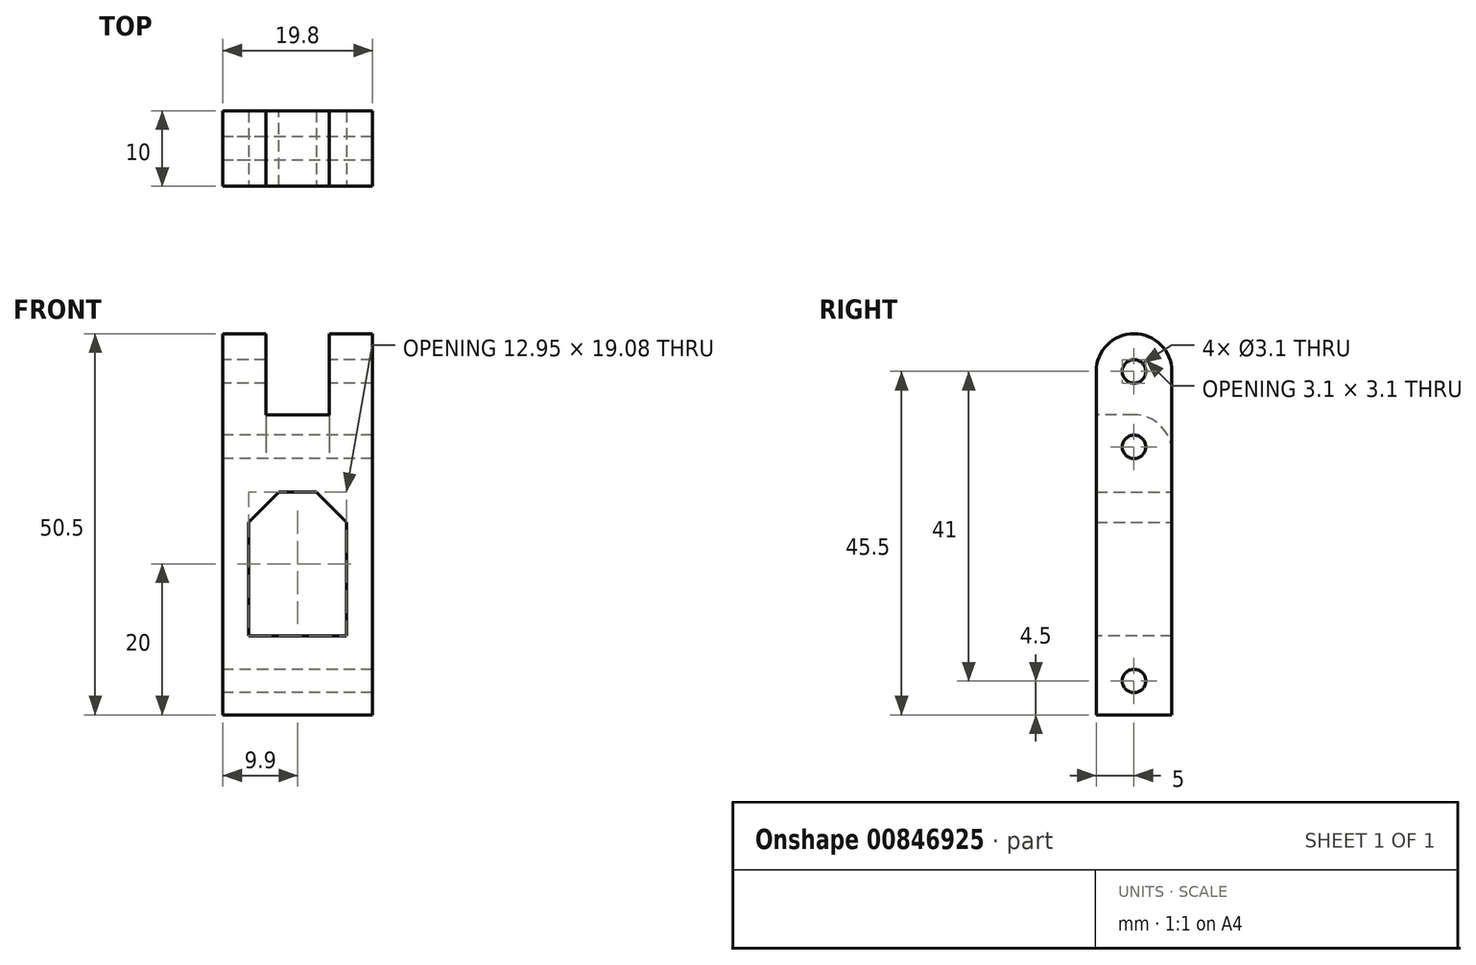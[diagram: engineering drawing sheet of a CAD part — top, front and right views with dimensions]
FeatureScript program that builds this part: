
annotation { "Feature Type Name" : "Feature", "Feature Type Description" : "" }
export const myFeature = defineFeature(function(context is Context, id is Id, definition is map)
    precondition{}
    {
        {
            var Q0;
            Q0=qCreatedBy(makeId("Right.planeOp"),FACE);
            var sketch = newSketch(context, id + "F0", { "sketchPlane" : qUnion([Q0])});
            skLineSegment(sketch, "E0.bottom", {"start": v(-5, -20) * mm, "end": v(5, -20) * mm});
            skLineSegment(sketch, "E0.top", {"start": v(-5, 25.5) * mm, "end": v(5, 25.5) * mm});
            skLineSegment(sketch, "E0.left", {"start": v(-5, -20) * mm, "end": v(-5, 25.5) * mm});
            skLineSegment(sketch, "E0.right", {"start": v(5, -20) * mm, "end": v(5, 25.5) * mm});
            skPoint(sketch, "E0.middle", {"position": v(0, 0) * mm});
            skArc(sketch, "E1", {"start": v(5, 25.5) * mm, "mid": v(0, 30.5) * mm, "end": v(-5, 25.5) * mm});
            skCircle(sketch, "E2", {"center": v(0, 25.5) * mm, "radius": 1.55 * mm});
            skCircle(sketch, "E3", {"center": v(0, -15.5) * mm, "radius": 1.55 * mm});
            skCircle(sketch, "E4", {"center": v(0, 15.5) * mm, "radius": 1.55 * mm});
            skSolve(sketch);
        }
        {
            var Q0;
            Q0 = qSketchRegion(id + "F0", true);
            var Q1;
            Q1 = qSketchRegion(id + "F2", true);
            extrude(context, id + "F1", {"entities" : qUnion([Q0, Q1]), "endBound" : BoundingType.SYMMETRIC, "depth" : 19.8 * mm, "offsetDistance" : 25 * mm});
        }
        {
            var Q0;
            Q0=makeQuery(id+"F1.opExtrude","SWEPT_FACE",FACE,{"disambiguationData":[OSD([sQuery(id+"F0.wireOp",EDGE,"E0.left")])]});
            var sketch = newSketch(context, id + "F2", { "sketchPlane" : qUnion([Q0])});
            skLineSegment(sketch, "E5.0", {"start": v(-9.9, 25.5) * mm, "end": v(-9.9, 30.5) * mm, "construction": true});
            skLineSegment(sketch, "E6.0", {"start": v(9.9, 25.5) * mm, "end": v(9.9, 30.5) * mm, "construction": true});
            skLineSegment(sketch, "E7", {"start": v(-9.9, 30.5) * mm, "end": v(9.9, 30.5) * mm, "construction": true});
            skLineSegment(sketch, "E8.bottom", {"start": v(4.2, 31.26) * mm, "end": v(-4.2, 31.26) * mm});
            skLineSegment(sketch, "E8.top", {"start": v(4.2, 19.74) * mm, "end": v(-4.2, 19.74) * mm});
            skLineSegment(sketch, "E8.left", {"start": v(4.2, 31.26) * mm, "end": v(4.2, 19.74) * mm});
            skLineSegment(sketch, "E8.right", {"start": v(-4.2, 31.26) * mm, "end": v(-4.2, 19.74) * mm});
            skPoint(sketch, "E8.middle", {"position": v(0, 25.5) * mm});
            skLineSegment(sketch, "E9.bottom", {"start": v(6.47, -9.54) * mm, "end": v(-6.47, -9.54) * mm});
            skLineSegment(sketch, "E9.top", {"start": v(6.47, 9.54) * mm, "end": v(-6.47, 9.54) * mm});
            skLineSegment(sketch, "E9.left", {"start": v(6.47, -9.54) * mm, "end": v(6.47, 9.54) * mm});
            skLineSegment(sketch, "E9.right", {"start": v(-6.47, -9.54) * mm, "end": v(-6.47, 9.54) * mm});
            skPoint(sketch, "E9.middle", {"position": v(0, 0) * mm});
            skSolve(sketch);
        }
        {
            var Q0;
            Q0 = qSketchRegion(id + "F2", true);
            extrude(context, id + "F3", {"entities" : qUnion([Q0]), "operationType" : NewBodyOperationType.REMOVE, "oppositeDirection" : true, "depth" : 25 * mm, "offsetDistance" : 25 * mm});
        }
        {
            var Q0;
            Q0=makeQuery(id+"F3.boolean.opBoolean","COPY",EDGE,{"derivedFrom":makeQuery(id+"F3.opExtrude","CAP_EDGE",EDGE,{"disambiguationData":[OSD([sQuery(id+"F2.wireOp",EDGE,"E8.top")])],"isStart":true})});
            var Q1;
            Q1=makeQuery(id+"F3.boolean.opBoolean","INTERSECT",EDGE,{"derivedFrom":[makeQuery(id+"F1.opExtrude","SWEPT_FACE",FACE,{"disambiguationData":[OSD([sQuery(id+"F0.wireOp",EDGE,"E0.right")])]}),makeQuery(id+"F3.opExtrude","SWEPT_FACE",FACE,{"disambiguationData":[OSD([sQuery(id+"F2.wireOp",EDGE,"E8.top")])]})]});
            fillet(context, id + "F4", {"entities" : qUnion([Q0, Q1]), "radius" : 5 * mm, "tangentPropagation" : true, "allowEdgeOverflow" : false});
        }
        {
            var Q0;
            Q0=makeQuery(id+"F3.boolean.opBoolean","COPY",EDGE,{"derivedFrom":makeQuery(id+"F3.opExtrude","SWEPT_EDGE",EDGE,{"disambiguationData":[OSD([sQuery(id+"F2.wireOp",EDGE,"E9.top"),sQuery(id+"F2.wireOp",EDGE,"E9.left")])]})});
            var Q1;
            Q1=makeQuery(id+"F3.boolean.opBoolean","COPY",EDGE,{"derivedFrom":makeQuery(id+"F3.opExtrude","SWEPT_EDGE",EDGE,{"disambiguationData":[OSD([sQuery(id+"F2.wireOp",EDGE,"E9.top"),sQuery(id+"F2.wireOp",EDGE,"E9.right")])]})});
            chamfer(context, id + "F5", {"entities" : qUnion([Q0, Q1]), "width" : 4 * mm, "tangentPropagation" : true});
        }
    });
